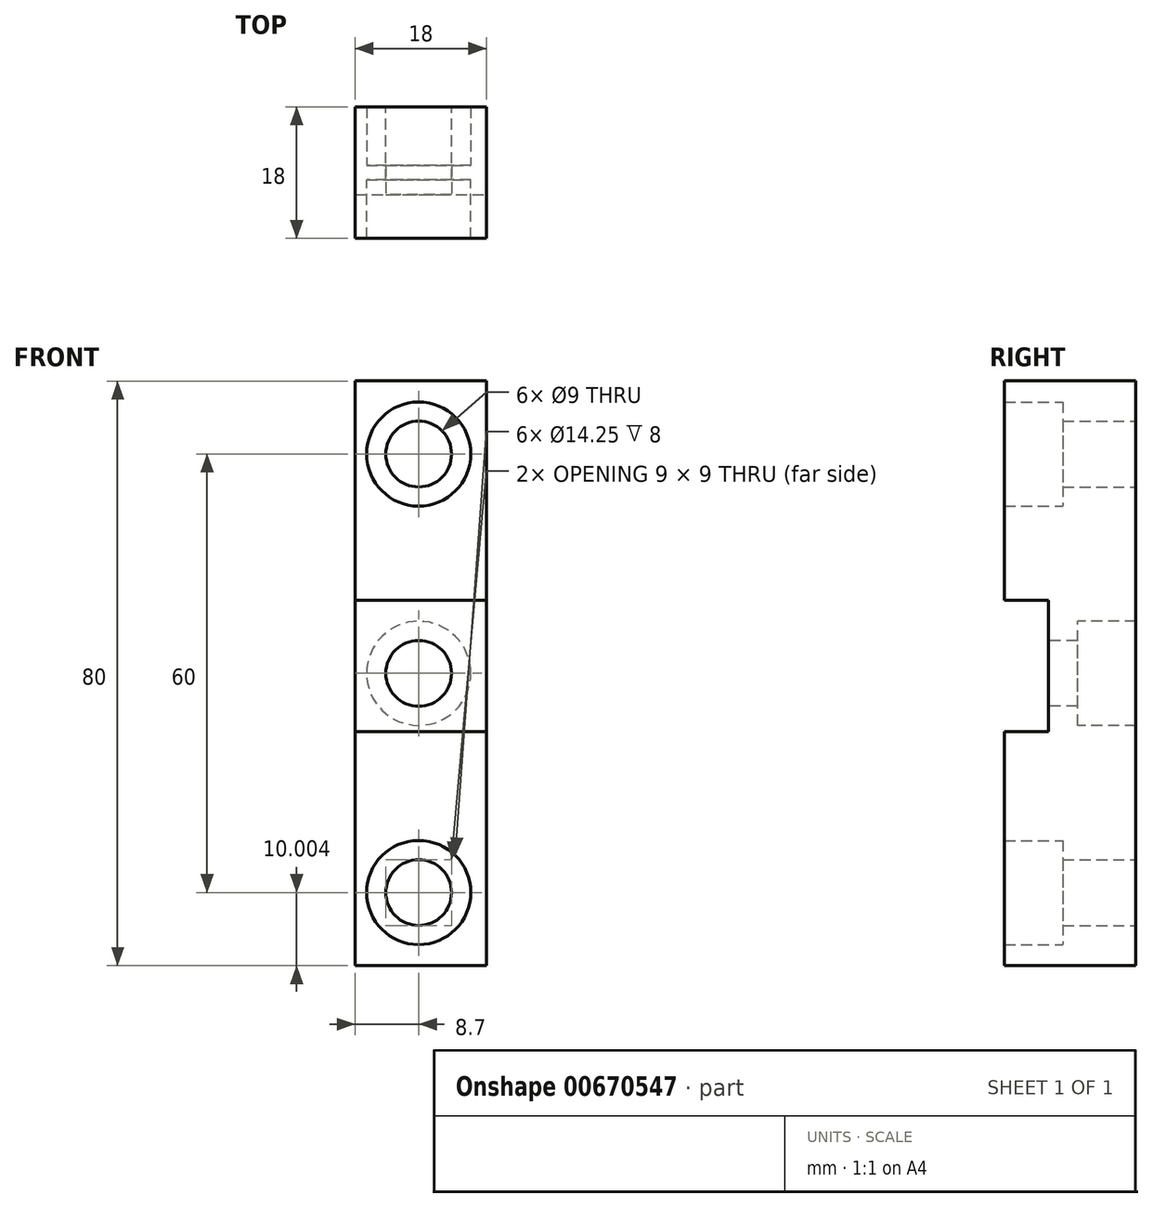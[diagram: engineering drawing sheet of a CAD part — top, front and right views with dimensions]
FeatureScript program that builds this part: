
annotation { "Feature Type Name" : "Feature", "Feature Type Description" : "" }
export const myFeature = defineFeature(function(context is Context, id is Id, definition is map)
    precondition{}
    {
        {
            var Q0;
            Q0=qCreatedBy(makeId("Front.planeOp"),FACE);
            var sketch = newSketch(context, id + "F0", { "sketchPlane" : qUnion([Q0])});
            skLineSegment(sketch, "E0.bottom", {"start": v(-8.7, 44.8) * mm, "end": v(9.3, 44.8) * mm});
            skLineSegment(sketch, "E0.top", {"start": v(-8.7, -35.2) * mm, "end": v(9.3, -35.2) * mm});
            skLineSegment(sketch, "E0.left", {"start": v(-8.7, 44.8) * mm, "end": v(-8.7, -35.2) * mm});
            skLineSegment(sketch, "E0.right", {"start": v(9.3, 44.8) * mm, "end": v(9.3, -35.2) * mm});
            skSolve(sketch);
        }
        {
            var Q0;
            Q0=makeQuery(id+"F0.imprint","IMPRINT",FACE,{"disambiguationData":[TD([[makeQuery(id+"F0.imprint","IMPRINT",EDGE,{"derivedFrom":sQuery(id+"F0.wireOp",EDGE,"E0.bottom")}),-1.0]])]});
            extrude(context, id + "F1", {"entities" : qUnion([Q0]), "depth" : 18 * mm, "offsetDistance" : 25 * mm});
        }
        {
            var Q0;
            Q0=makeQuery(id+"F1.opExtrude","CAP_FACE",FACE,{"disambiguationData":[OSD([sQuery(id+"F0.wireOp",EDGE,"E0.bottom"),sQuery(id+"F0.wireOp",EDGE,"E0.top"),sQuery(id+"F0.wireOp",EDGE,"E0.left"),sQuery(id+"F0.wireOp",EDGE,"E0.right")])],"isStart":false});
            var sketch = newSketch(context, id + "F2", { "sketchPlane" : qUnion([Q0])});
            skPoint(sketch, "E1", {"position": v(0, 34.8) * mm});
            skPoint(sketch, "E2", {"position": v(0, -25.2) * mm});
            skSolve(sketch);
        }
        {
            var Q0;
            Q0=sQuery(id+"F2.wireOp",VERTEX,"E1");
            var Q1;
            Q1=sQuery(id+"F2.wireOp",VERTEX,"E2");
            var Q2;
            Q2=makeQuery(id+"F1.opExtrude","SWEPT_BODY",BODY,{"disambiguationData":[OSD([sQuery(id+"F0.wireOp",EDGE,"E0.bottom"),sQuery(id+"F0.wireOp",EDGE,"E0.top"),sQuery(id+"F0.wireOp",EDGE,"E0.left"),sQuery(id+"F0.wireOp",EDGE,"E0.right")])]});
            hole(context, id + "F3", {"style" : HoleStyle.C_BORE, "endStyle" : HoleEndStyle.BLIND, "standardTappedOrClearance" : lookupTablePath({ "fit" : "Normal", "standard" : "ISO", "size" : "M8", "type" : "Clearance" }), "standardBlindInLast" : lookupTablePath({ "fit" : "Normal", "standard" : "ISO", "size" : "M8", "type" : "Clearance" }), "holeDiameter" : 9 * mm, "cBoreDiameter" : 14.25 * mm, "cBoreDepth" : 8 * mm, "majorDiameter" : 8 * mm, "holeDepth" : 18.75 * mm, "isTappedThrough" : true, "tappedDepth" : 15 * mm, "tapClearance" : 3, "locations" : qUnion([Q0, Q1]), "scope" : qUnion([Q2]), "startStyle" : HoleStartStyle.PART});
        }
        {
            var Q0;
            Q0=makeQuery(id+"F1.opExtrude","CAP_FACE",FACE,{"disambiguationData":[OSD([sQuery(id+"F0.wireOp",EDGE,"E0.bottom"),sQuery(id+"F0.wireOp",EDGE,"E0.top"),sQuery(id+"F0.wireOp",EDGE,"E0.left"),sQuery(id+"F0.wireOp",EDGE,"E0.right")])],"isStart":false});
            var sketch = newSketch(context, id + "F4", { "sketchPlane" : qUnion([Q0])});
            skLineSegment(sketch, "E3.bottom", {"start": v(-8.7, 14.8) * mm, "end": v(9.3, 14.8) * mm});
            skLineSegment(sketch, "E3.top", {"start": v(-8.7, -3.2) * mm, "end": v(9.3, -3.2) * mm});
            skLineSegment(sketch, "E3.left", {"start": v(-8.7, 14.8) * mm, "end": v(-8.7, -3.2) * mm});
            skLineSegment(sketch, "E3.right", {"start": v(9.3, 14.8) * mm, "end": v(9.3, -3.2) * mm});
            skSolve(sketch);
        }
        {
            var Q0;
            Q0=makeQuery(id+"F4.imprint","IMPRINT",FACE,{"disambiguationData":[TD([[makeQuery(id+"F4.imprint","IMPRINT",EDGE,{"derivedFrom":sQuery(id+"F4.wireOp",EDGE,"E3.bottom")}),-1.0]])]});
            extrude(context, id + "F5", {"entities" : qUnion([Q0]), "operationType" : NewBodyOperationType.REMOVE, "oppositeDirection" : true, "depth" : 6 * mm, "offsetDistance" : 25 * mm});
        }
        {
            var Q0;
            Q0=makeQuery(id+"F1.opExtrude","CAP_FACE",FACE,{"disambiguationData":[OSD([sQuery(id+"F0.wireOp",EDGE,"E0.bottom"),sQuery(id+"F0.wireOp",EDGE,"E0.top"),sQuery(id+"F0.wireOp",EDGE,"E0.left"),sQuery(id+"F0.wireOp",EDGE,"E0.right")])],"isStart":true});
            var sketch = newSketch(context, id + "F6", { "sketchPlane" : qUnion([Q0])});
            skPoint(sketch, "E4", {"position": v(0, 4.8) * mm});
            skSolve(sketch);
        }
        {
            var Q0;
            Q0=sQuery(id+"F6.wireOp",VERTEX,"E4");
            var Q1;
            Q1=makeQuery(id+"F1.opExtrude","SWEPT_BODY",BODY,{"disambiguationData":[OSD([sQuery(id+"F0.wireOp",EDGE,"E0.bottom"),sQuery(id+"F0.wireOp",EDGE,"E0.top"),sQuery(id+"F0.wireOp",EDGE,"E0.left"),sQuery(id+"F0.wireOp",EDGE,"E0.right")])]});
            hole(context, id + "F7", {"style" : HoleStyle.C_BORE, "endStyle" : HoleEndStyle.BLIND, "standardTappedOrClearance" : lookupTablePath({ "fit" : "Normal", "standard" : "ISO", "size" : "M8", "type" : "Clearance" }), "standardBlindInLast" : lookupTablePath({ "fit" : "Normal", "standard" : "ISO", "size" : "M8", "type" : "Clearance" }), "holeDiameter" : 9 * mm, "cBoreDiameter" : 14.25 * mm, "cBoreDepth" : 8 * mm, "majorDiameter" : 5 * mm, "holeDepth" : 18.75 * mm, "isTappedThrough" : true, "tappedDepth" : 15 * mm, "tapClearance" : 3, "locations" : qUnion([Q0]), "scope" : qUnion([Q1]), "startStyle" : HoleStartStyle.PART});
        }
    });
